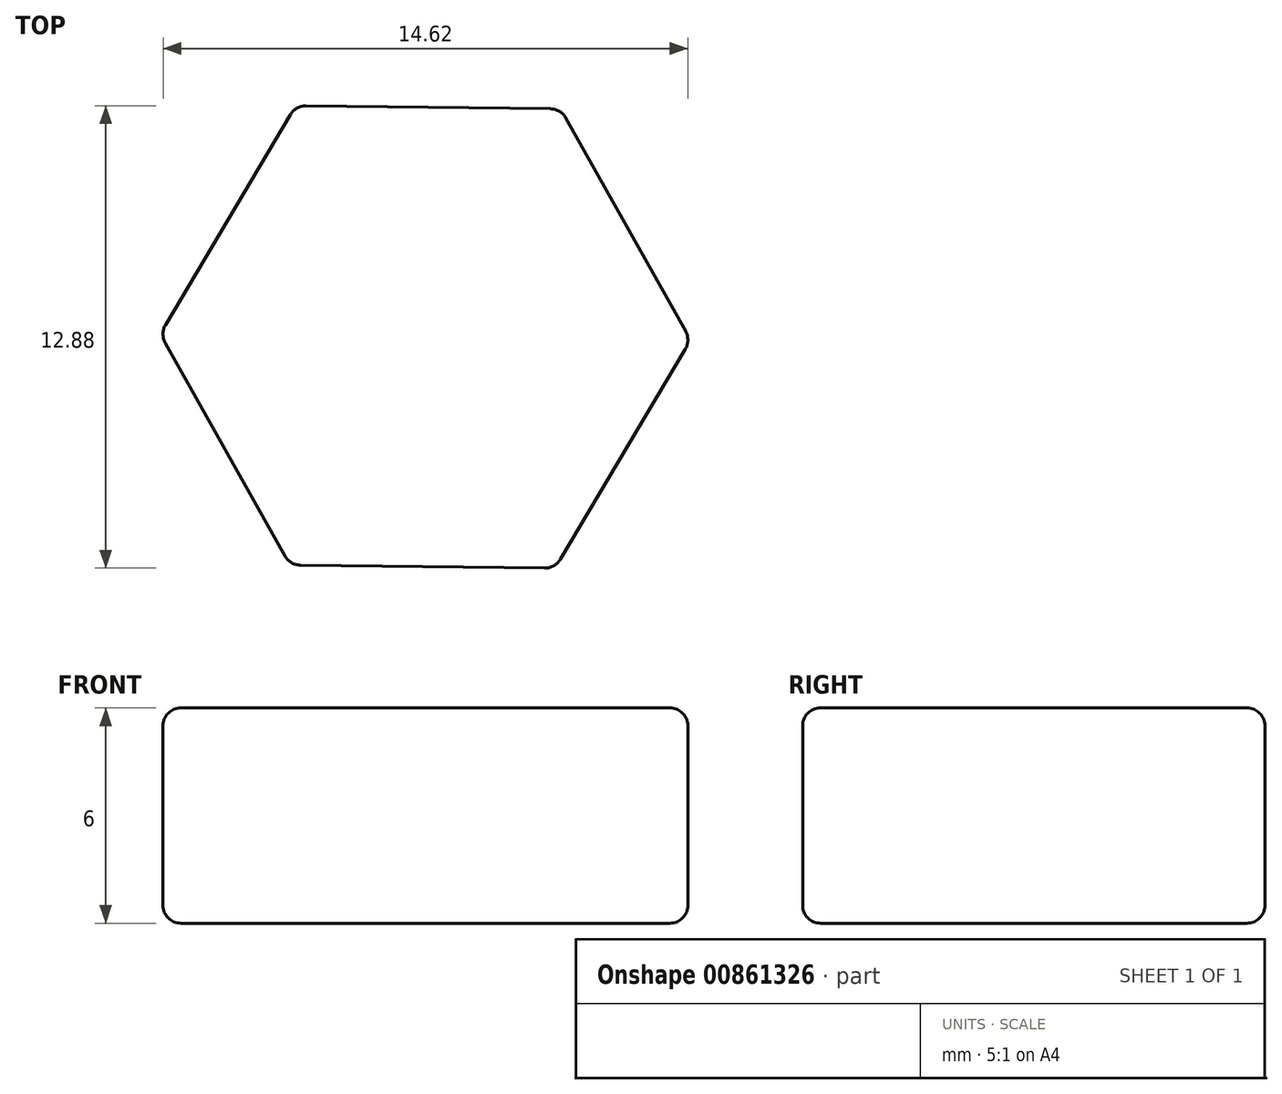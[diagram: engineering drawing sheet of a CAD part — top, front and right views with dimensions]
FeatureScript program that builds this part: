
annotation { "Feature Type Name" : "Feature", "Feature Type Description" : "" }
export const myFeature = defineFeature(function(context is Context, id is Id, definition is map)
    precondition{}
    {
        {
            var Q0;
            Q0=qCreatedBy(makeId("Top.planeOp"),FACE);
            var sketch = newSketch(context, id + "F0", { "sketchPlane" : qUnion([Q0])});
            skCircle(sketch, "E0.cCircle", {"center": v(-17.11, 11.09) * mm, "radius": 6.4 * mm, "construction": true});
            skLineSegment(sketch, "E0.0", {"start": v(-13.34, 17.44) * mm, "end": v(-9.72, 11) * mm});
            skLineSegment(sketch, "E0.1", {"start": v(-9.72, 11) * mm, "end": v(-13.5, 4.64) * mm});
            skLineSegment(sketch, "E0.2", {"start": v(-13.5, 4.64) * mm, "end": v(-20.88, 4.73) * mm});
            skLineSegment(sketch, "E0.3", {"start": v(-20.88, 4.73) * mm, "end": v(-24.5, 11.18) * mm});
            skLineSegment(sketch, "E0.4", {"start": v(-24.5, 11.18) * mm, "end": v(-20.73, 17.53) * mm});
            skLineSegment(sketch, "E0.5", {"start": v(-20.73, 17.53) * mm, "end": v(-13.34, 17.44) * mm});
            skPoint(sketch, "E0.0.midPoint", {"position": v(-11.53, 14.22) * mm});
            skSolve(sketch);
        }
        {
            var Q0;
            Q0 = qSketchRegion(id + "F0", true);
            extrude(context, id + "F1", {"entities" : qUnion([Q0]), "depth" : 6 * mm, "offsetDistance" : 25 * mm});
        }
        {
            var Q0;
            Q0=makeQuery(id+"F1.opExtrude","CAP_FACE",FACE,{"disambiguationData":[OSD([sQuery(id+"F0.wireOp",EDGE,"E0.0"),sQuery(id+"F0.wireOp",EDGE,"E0.1"),sQuery(id+"F0.wireOp",EDGE,"E0.2"),sQuery(id+"F0.wireOp",EDGE,"E0.3"),sQuery(id+"F0.wireOp",EDGE,"E0.4"),sQuery(id+"F0.wireOp",EDGE,"E0.5")])],"isStart":false});
            var Q1;
            Q1=makeQuery(id+"F1.opExtrude","CAP_FACE",FACE,{"disambiguationData":[OSD([sQuery(id+"F0.wireOp",EDGE,"E0.0"),sQuery(id+"F0.wireOp",EDGE,"E0.1"),sQuery(id+"F0.wireOp",EDGE,"E0.2"),sQuery(id+"F0.wireOp",EDGE,"E0.3"),sQuery(id+"F0.wireOp",EDGE,"E0.4"),sQuery(id+"F0.wireOp",EDGE,"E0.5")])],"isStart":true});
            var Q2;
            Q2=makeQuery(id+"F1.opExtrude","SWEPT_FACE",FACE,{"disambiguationData":[OSD([sQuery(id+"F0.wireOp",EDGE,"E0.2")])]});
            var Q3;
            Q3=makeQuery(id+"F1.opExtrude","SWEPT_FACE",FACE,{"disambiguationData":[OSD([sQuery(id+"F0.wireOp",EDGE,"E0.1")])]});
            var Q4;
            Q4=makeQuery(id+"F1.opExtrude","SWEPT_FACE",FACE,{"disambiguationData":[OSD([sQuery(id+"F0.wireOp",EDGE,"E0.3")])]});
            var Q5;
            Q5=makeQuery(id+"F1.opExtrude","SWEPT_FACE",FACE,{"disambiguationData":[OSD([sQuery(id+"F0.wireOp",EDGE,"E0.4")])]});
            var Q6;
            Q6=makeQuery(id+"F1.opExtrude","SWEPT_FACE",FACE,{"disambiguationData":[OSD([sQuery(id+"F0.wireOp",EDGE,"E0.5")])]});
            fillet(context, id + "F2", {"entities" : qUnion([Q0, Q1, Q2, Q3, Q4, Q5, Q6]), "radius" : 0.5 * mm, "tangentPropagation" : true, "allowEdgeOverflow" : false});
        }
    });
